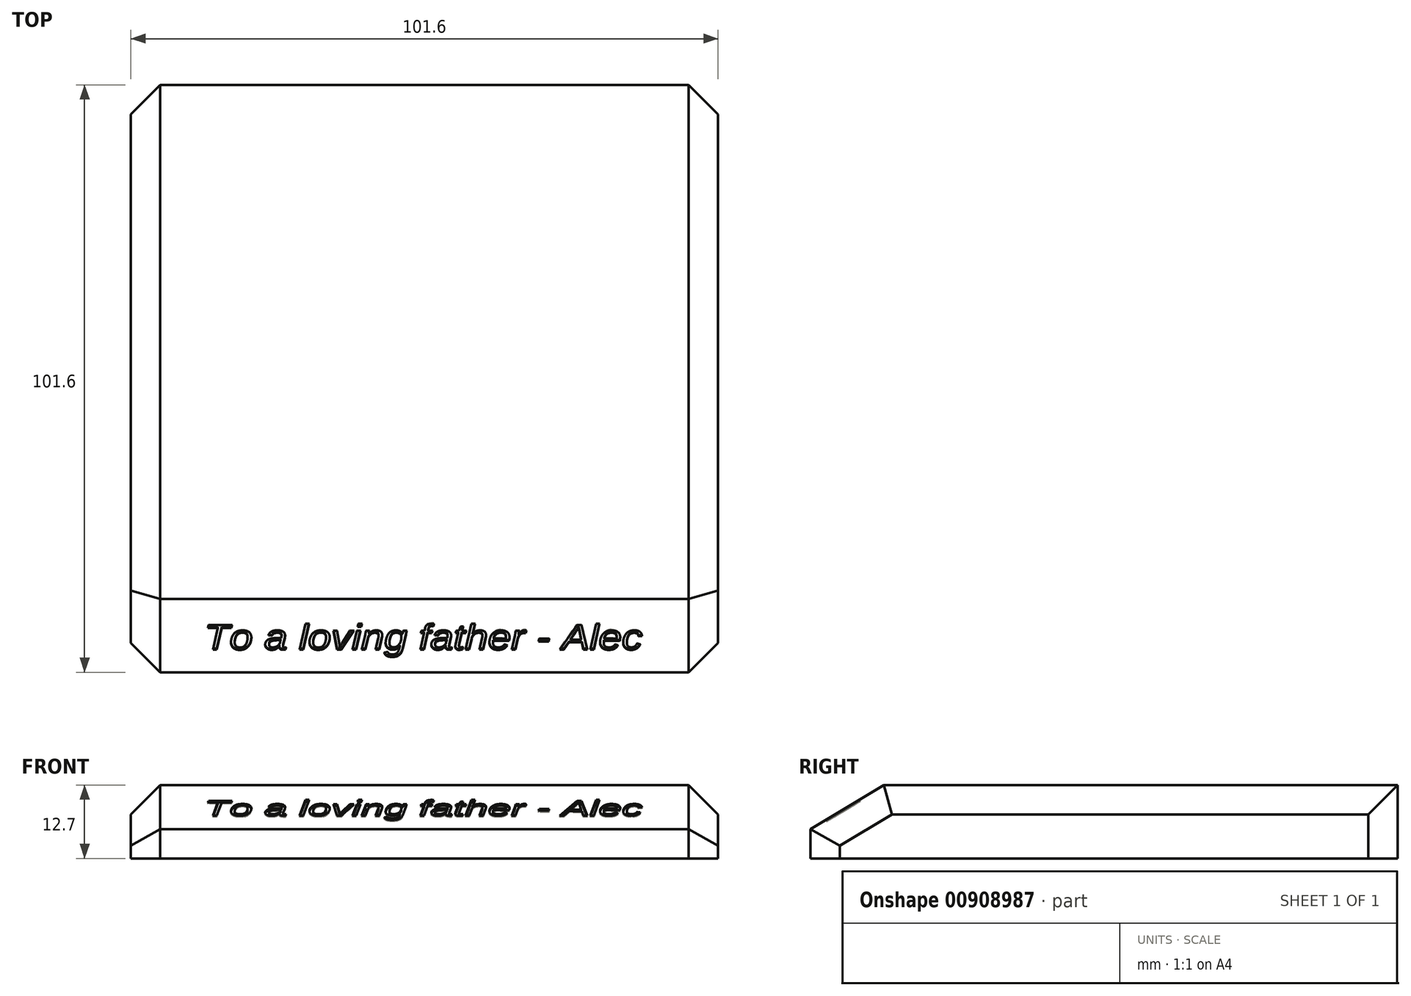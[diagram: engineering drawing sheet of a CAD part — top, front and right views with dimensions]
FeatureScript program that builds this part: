
annotation { "Feature Type Name" : "Feature", "Feature Type Description" : "" }
export const myFeature = defineFeature(function(context is Context, id is Id, definition is map)
    precondition{}
    {
        {
            var Q0;
            Q0=qCreatedBy(makeId("Top.planeOp"),FACE);
            var sketch = newSketch(context, id + "F0", { "sketchPlane" : qUnion([Q0])});
            skLineSegment(sketch, "E0.bottom", {"start": v(50.8, 50.8) * mm, "end": v(-50.8, 50.8) * mm});
            skLineSegment(sketch, "E0.top", {"start": v(50.8, -50.8) * mm, "end": v(-50.8, -50.8) * mm});
            skLineSegment(sketch, "E0.left", {"start": v(50.8, 50.8) * mm, "end": v(50.8, -50.8) * mm});
            skLineSegment(sketch, "E0.right", {"start": v(-50.8, 50.8) * mm, "end": v(-50.8, -50.8) * mm});
            skPoint(sketch, "E0.middle", {"position": v(0, 0) * mm});
            skSolve(sketch);
        }
        {
            var Q0;
            Q0=makeQuery(id+"F0.imprint","IMPRINT",FACE,{"disambiguationData":[TD([[makeQuery(id+"F0.imprint","IMPRINT",EDGE,{"derivedFrom":sQuery(id+"F0.wireOp",EDGE,"E0.bottom")}),1.0]])]});
            extrude(context, id + "F1", {"entities" : qUnion([Q0]), "depth" : 12.7 * mm, "offsetDistance" : 25.4 * mm});
        }
        {
            var Q0;
            Q0=makeQuery(id+"F1.opExtrude","CAP_EDGE",EDGE,{"disambiguationData":[OSD([sQuery(id+"F0.wireOp",EDGE,"E0.top")])],"isStart":false});
            chamfer(context, id + "F2", {"entities" : qUnion([Q0]), "chamferType" : ChamferType.TWO_OFFSETS, "width1" : 7.62 * mm, "oppositeDirection" : false, "width2" : 12.7 * mm, "tangentPropagation" : true});
        }
        {
            var Q0;
            Q0=makeQuery(id+"F1.opExtrude","SWEPT_EDGE",EDGE,{"disambiguationData":[OSD([sQuery(id+"F0.wireOp",EDGE,"E0.top"),sQuery(id+"F0.wireOp",EDGE,"E0.right")])]});
            var Q1;
            Q1=makeQuery(id+"F2.opChamfer","BLEND_EDGE",EDGE,{"blendedFrom":[makeQuery(id+"F1.opExtrude","CAP_EDGE",EDGE,{"disambiguationData":[OSD([sQuery(id+"F0.wireOp",EDGE,"E0.top")])],"isStart":false}),makeQuery(id+"F1.opExtrude","SWEPT_FACE",FACE,{"disambiguationData":[OSD([sQuery(id+"F0.wireOp",EDGE,"E0.right")])]})],"blendedInto":[makeQuery(id+"F1.opExtrude","SWEPT_FACE",FACE,{"disambiguationData":[OSD([sQuery(id+"F0.wireOp",EDGE,"E0.right")])]})]});
            var Q2;
            Q2=makeQuery(id+"F1.opExtrude","CAP_EDGE",EDGE,{"disambiguationData":[OSD([sQuery(id+"F0.wireOp",EDGE,"E0.right")])],"isStart":false});
            var Q3;
            Q3=makeQuery(id+"F1.opExtrude","SWEPT_EDGE",EDGE,{"disambiguationData":[OSD([sQuery(id+"F0.wireOp",EDGE,"E0.top"),sQuery(id+"F0.wireOp",EDGE,"E0.left")])]});
            var Q4;
            Q4=makeQuery(id+"F2.opChamfer","BLEND_EDGE",EDGE,{"blendedFrom":[makeQuery(id+"F1.opExtrude","CAP_EDGE",EDGE,{"disambiguationData":[OSD([sQuery(id+"F0.wireOp",EDGE,"E0.top")])],"isStart":false}),makeQuery(id+"F1.opExtrude","SWEPT_FACE",FACE,{"disambiguationData":[OSD([sQuery(id+"F0.wireOp",EDGE,"E0.left")])]})],"blendedInto":[makeQuery(id+"F1.opExtrude","SWEPT_FACE",FACE,{"disambiguationData":[OSD([sQuery(id+"F0.wireOp",EDGE,"E0.left")])]})]});
            var Q5;
            Q5=makeQuery(id+"F1.opExtrude","CAP_EDGE",EDGE,{"disambiguationData":[OSD([sQuery(id+"F0.wireOp",EDGE,"E0.left")])],"isStart":false});
            var Q6;
            Q6=makeQuery(id+"F1.opExtrude","SWEPT_EDGE",EDGE,{"disambiguationData":[OSD([sQuery(id+"F0.wireOp",EDGE,"E0.bottom"),sQuery(id+"F0.wireOp",EDGE,"E0.left")])]});
            var Q7;
            Q7=makeQuery(id+"F1.opExtrude","SWEPT_EDGE",EDGE,{"disambiguationData":[OSD([sQuery(id+"F0.wireOp",EDGE,"E0.bottom"),sQuery(id+"F0.wireOp",EDGE,"E0.right")])]});
            chamfer(context, id + "F3", {"entities" : qUnion([Q0, Q1, Q2, Q3, Q4, Q5, Q6, Q7]), "width" : 5.08 * mm, "tangentPropagation" : true});
        }
        {
            var Q0;
            Q0=makeQuery(id+"F2.opChamfer","BLEND_FACE",FACE,{"disambiguationData":[OSD([sQuery(id+"F0.wireOp",EDGE,"E0.top")])]});
            var sketch = newSketch(context, id + "F4", { "sketchPlane" : qUnion([Q0])});
            skText(sketch, "E1", { "text": "To a loving father - Alec", "fontName": "Arimo-Italic.ttf"});
            const initialGuessF4  = {"E1": [-0.0381, -0.03638, 1, 0, 0.00517]};
            skSetInitialGuess(sketch, initialGuessF4);
            skSolve(sketch);
        }
        {
            var Q0;
            Q0=qSketchRegion(id+"F4",true);
            extrude(context, id + "F5", {"entities" : qUnion([Q0]), "operationType" : NewBodyOperationType.REMOVE, "oppositeDirection" : true, "depth" : 0.3 * mm, "offsetDistance" : 25.4 * mm});
        }
    });
